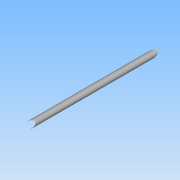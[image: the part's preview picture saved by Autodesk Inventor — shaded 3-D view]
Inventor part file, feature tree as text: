
AUTODESK INVENTOR PART (.ipt)
format: ipt  version: 2015 (Build 190159000, 159)  size: 65,536 bytes
history: native  units: mm
features: extrude x1, sketch x1
ambient origin geometry x8: Origin, YZ Plane, XZ Plane, XY Plane, X Axis, Y Axis, Z Axis, Center Point
bodies: Solid1 (feature_tree)
feature tree (2):
  extrude  "Extrusion1"  Depth=136.0mm TaperAngle=0.0deg
  sketch  "Sketch1"  dims[d0=5.0mm d1=136.0mm d2=0.0mm]
